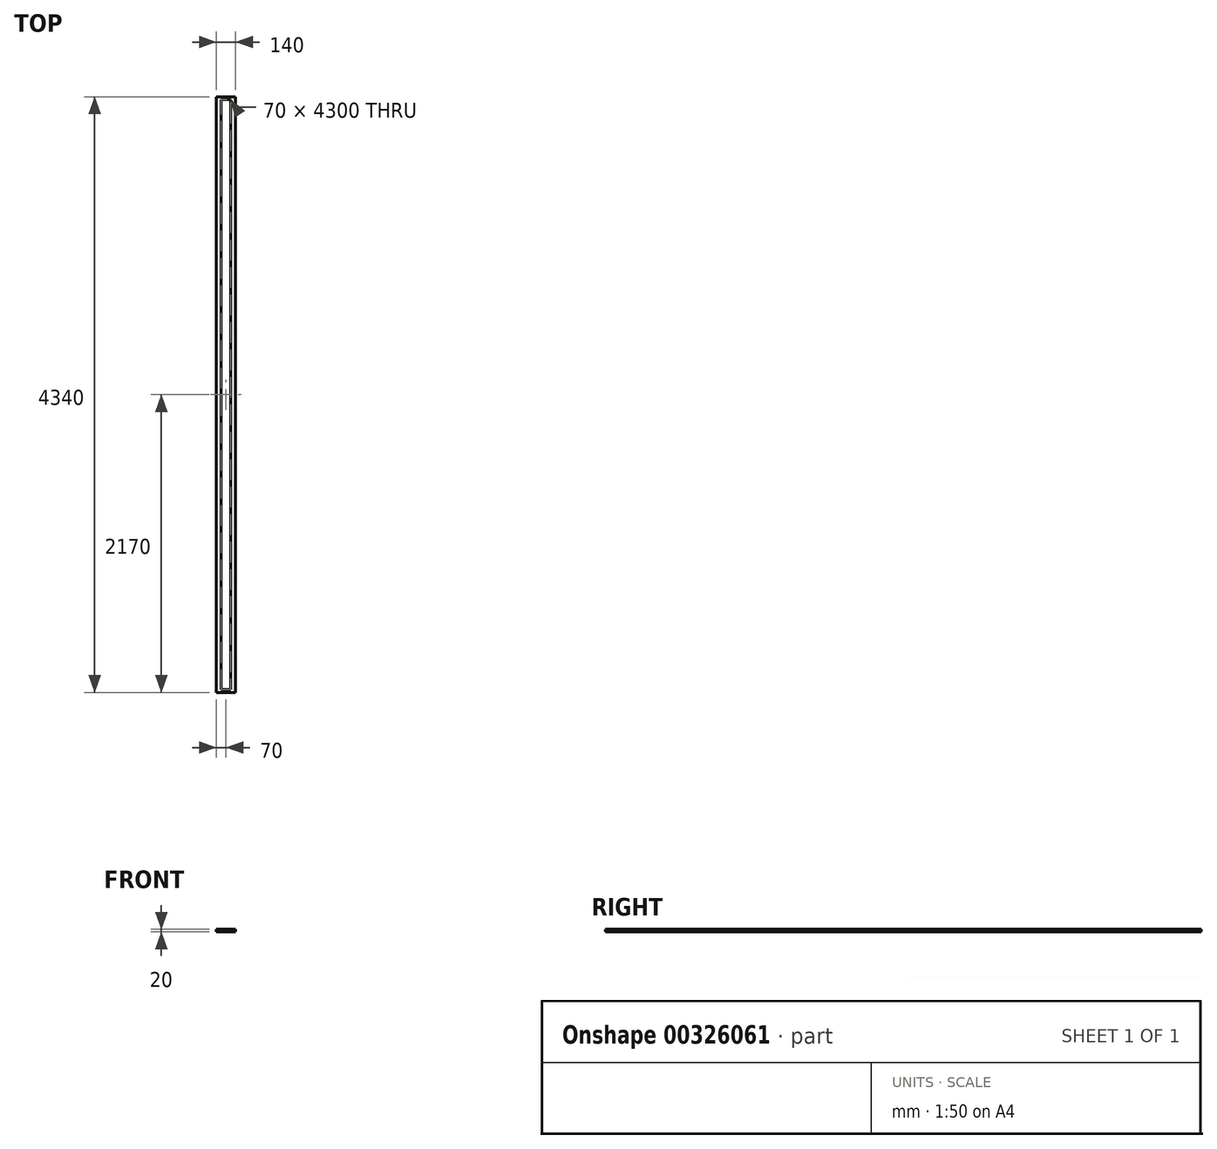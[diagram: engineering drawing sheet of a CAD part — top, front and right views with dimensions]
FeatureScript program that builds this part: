
annotation { "Feature Type Name" : "Feature", "Feature Type Description" : "" }
export const myFeature = defineFeature(function(context is Context, id is Id, definition is map)
    precondition{}
    {
        {
            var Q0;
            Q0=qCreatedBy(makeId("Top.planeOp"),FACE);
            var sketch = newSketch(context, id + "F0", { "sketchPlane" : qUnion([Q0])});
            skLineSegment(sketch, "E0", {"start": v(-70, 0) * mm, "end": v(70, 0) * mm, "construction": true});
            skLineSegment(sketch, "E1.bottom", {"start": v(-70, 0) * mm, "end": v(-35, 0) * mm});
            skLineSegment(sketch, "E1.top", {"start": v(-70, 4340) * mm, "end": v(-35, 4340) * mm});
            skLineSegment(sketch, "E1.left", {"start": v(-70, 0) * mm, "end": v(-70, 4340) * mm});
            skLineSegment(sketch, "E1.right", {"start": v(-35, 0) * mm, "end": v(-35, 4340) * mm});
            skLineSegment(sketch, "E2.bottom", {"start": v(70, 0) * mm, "end": v(35, 0) * mm});
            skLineSegment(sketch, "E2.top", {"start": v(70, 4340) * mm, "end": v(35, 4340) * mm});
            skLineSegment(sketch, "E2.left", {"start": v(70, 0) * mm, "end": v(70, 4340) * mm});
            skLineSegment(sketch, "E2.right", {"start": v(35, 0) * mm, "end": v(35, 4340) * mm});
            skSolve(sketch);
        }
        {
            var Q0;
            Q0=qSketchRegion(id+"F0",true);
            extrude(context, id + "F1", {"entities" : qUnion([Q0]), "depth" : 20 * mm});
        }
        {
            var Q0;
            Q0=makeQuery(id+"F1.opExtrude","SWEPT_FACE",FACE,{"disambiguationData":[OSD([sQuery(id+"F0.wireOp",EDGE,"E1.bottom")])]});
            var sketch = newSketch(context, id + "F2", { "sketchPlane" : qUnion([Q0])});
            skPoint(sketch, "E3.0", {"position": v(-35, 20) * mm});
            skPoint(sketch, "E4.0", {"position": v(35, 0) * mm});
            skLineSegment(sketch, "E5.bottom", {"start": v(-35, 20) * mm, "end": v(35, 20) * mm});
            skLineSegment(sketch, "E5.top", {"start": v(-35, 0) * mm, "end": v(35, 0) * mm});
            skLineSegment(sketch, "E5.left", {"start": v(-35, 20) * mm, "end": v(-35, 0) * mm});
            skLineSegment(sketch, "E5.right", {"start": v(35, 20) * mm, "end": v(35, 0) * mm});
            skSolve(sketch);
        }
        {
            var Q0;
            Q0=makeQuery(id+"F1.opExtrude","SWEPT_FACE",FACE,{"disambiguationData":[OSD([sQuery(id+"F0.wireOp",EDGE,"E2.top")])]});
            var sketch = newSketch(context, id + "F3", { "sketchPlane" : qUnion([Q0])});
            skPoint(sketch, "E6.0", {"position": v(35, 0) * mm});
            skPoint(sketch, "E7.0", {"position": v(-35, 20) * mm});
            skLineSegment(sketch, "E8.bottom", {"start": v(-35, 20) * mm, "end": v(35, 20) * mm});
            skLineSegment(sketch, "E8.top", {"start": v(-35, 0) * mm, "end": v(35, 0) * mm});
            skLineSegment(sketch, "E8.left", {"start": v(-35, 20) * mm, "end": v(-35, 0) * mm});
            skLineSegment(sketch, "E8.right", {"start": v(35, 20) * mm, "end": v(35, 0) * mm});
            skSolve(sketch);
        }
        {
            var Q0;
            Q0=makeQuery(id+"F2.imprint","IMPRINT",FACE,{"disambiguationData":[TD([[makeQuery(id+"F2.imprint","IMPRINT",EDGE,{"derivedFrom":sQuery(id+"F2.wireOp",EDGE,"E5.bottom")}),-1.0]])]});
            extrude(context, id + "F4", {"entities" : qUnion([Q0]), "operationType" : NewBodyOperationType.ADD, "oppositeDirection" : true, "depth" : 20 * mm});
        }
        {
            var Q0;
            Q0=makeQuery(id+"F3.imprint","IMPRINT",FACE,{"disambiguationData":[TD([[makeQuery(id+"F3.imprint","IMPRINT",EDGE,{"derivedFrom":sQuery(id+"F3.wireOp",EDGE,"E8.bottom")}),-1.0]])]});
            extrude(context, id + "F5", {"entities" : qUnion([Q0]), "operationType" : NewBodyOperationType.ADD, "oppositeDirection" : true, "depth" : 20 * mm});
        }
    });
